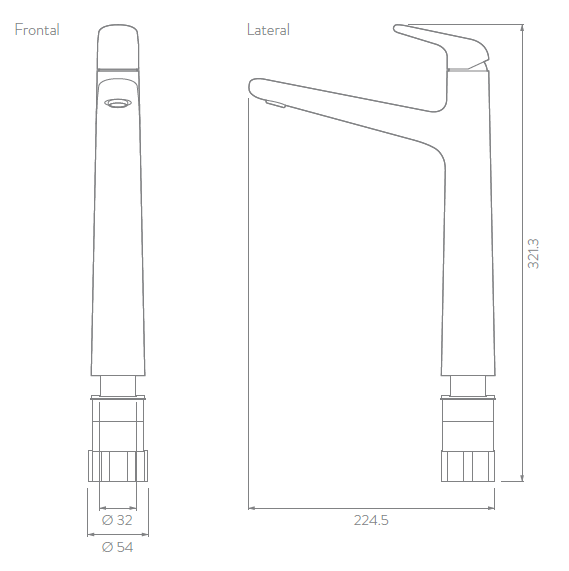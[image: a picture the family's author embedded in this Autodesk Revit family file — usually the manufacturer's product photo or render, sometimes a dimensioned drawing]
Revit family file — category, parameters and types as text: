
# Revit family: LQ1045551_Grifería para Lavamanos Monocontrol Liquid Niquel Media
name_source: partatom
category: Plumbing Fixtures
units: mm (PartAtom-declared; Revit-internal decimal feet)

## family parameters
Always vertical = Yes
Cut with Voids When Loaded = No
OmniClass Number = 23.31.11.00
OmniClass Title = Faucets
Part Type = Normal
Room Calculation Point = No
Round Connector Dimension = Use Diameter
Shared = No
Work Plane-Based = No

## types (1)
- LQ1045551_Grifería para Lavamanos Monocontrol Liquid Niquel Media
    Acabado = Corona_Niquel
    Alto = 192 mm  [stored 0.629921 ft]
    Altura de la grifería = Media
    Ancho = 54 mm  [stored 0.177165 ft]
    Capacidad de flujo = 60 psi: 4,86 L/min.
    Colección = Liquid
    Consumo de agua = 5.7 lt
    Creado por = IDD
    Description = La línea de griferías, duchas y accesorios Liquid se inspira en la tensión superficial del agua y en cómo esta crea formas armoniosas adaptándose al ambiente. Al igual que el agua, las superficies de las griferías Liquid juegan con la luz y los reflejos que fluyen alrededorde sus formas, sus líneas continuas y simplicidad formal proporcionan la ventaja práctica y limpieza sin esfuerzo.
Incluye la tecnología Ecostream, de ahorro de agua; y la tecnología ThermoControl, de control más preciso de la temperatura.
Incluye apertura con accionamiento central en frío que evita el encendido automático de calentadores y calderas ahorrando energía; además, es de fácil limpieza gracias al diseño que evita la acumulación de impurezas, es resistente a la corrosión, pelado y decoloración por agua y tiene recubrimientos no tóxicos.
    Fecha de creación = 09/10/2020
    Garantía = 30 años en estructura
    Garantías de otros componentes = 5 años en acabados
    Incluye = Cuerpo, Manija
    Linea = Liquid
    Longitud = 181 mm  [stored 0.593832 ft]
    Material = Metálico
    Peso  Bruto = 1.480 g. - 3,26 lb.
    Peso neto = 1.320 g. - 2,91 lb.
    Presión máxima recomendada = 125 psi (860 Kpa)
    Presión mínima recomendada = 20 psi (140 Kpa)
    Productos compatibles = Lavamanos de mesón integrado, Lavamanos para sobreponer, Lavamanos para incrustar
Lavamanos de pedestal, Lavamanos de semipedestal,Lavamanos de colgar
    Resistencia = Resistente a la corrosión pelado y decoloración por agua
    Sistema de accionamiento = Palanca monocontrol
    Tecnologías = DuraCrome EcoStream ThermoControl
    Temperaturas máxima de trabajo = 71°C / 159,8°F
    Temperaturas mínima de trabajo = 5°C / 41 °F
    Tipo de Chorro = Espumoso
    Tipo de Grifería = Monocontrol
    Tipo de manija/accionamiento = Palanca
    URL = https://corona.co
    Uso = Residencial
    Vida útil = 500.000 ciclos.

note: [stored X ft] marks values corroborated as IEEE doubles in the binary element streams (Revit-internal decimal feet)

## geometry (parser evidence)
native form markers: Sweep x8
no freeform markers — native parametric forms only
